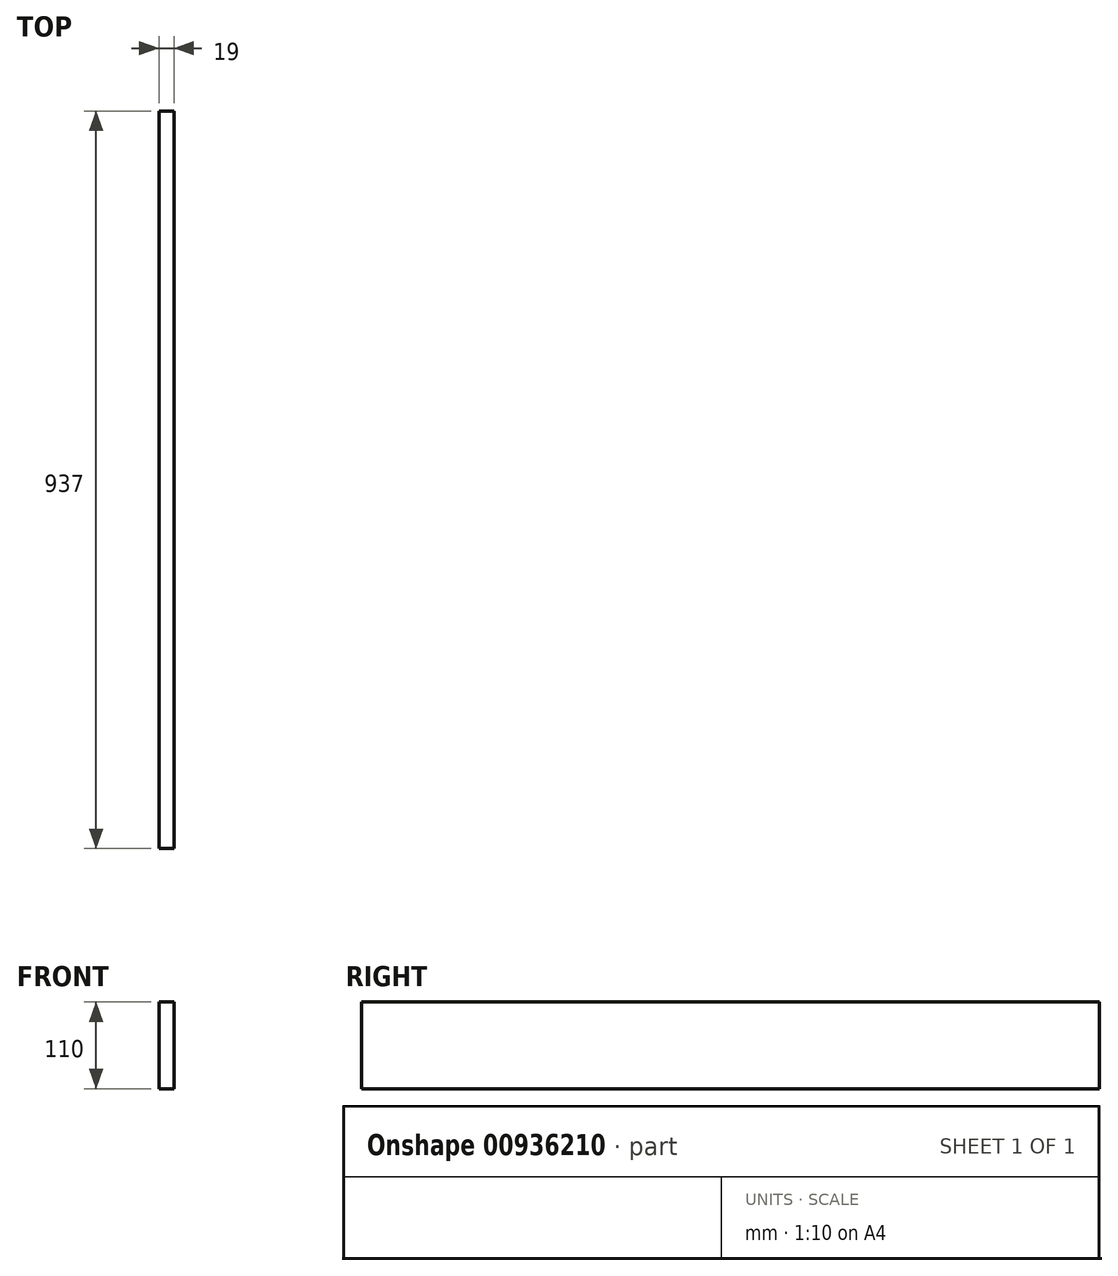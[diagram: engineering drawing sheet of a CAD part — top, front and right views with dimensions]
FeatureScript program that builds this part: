
annotation { "Feature Type Name" : "Feature", "Feature Type Description" : "" }
export const myFeature = defineFeature(function(context is Context, id is Id, definition is map)
    precondition{}
    {
        {
            var Q0;
            Q0=qCreatedBy(makeId("Front.planeOp"),FACE);
            var sketch = newSketch(context, id + "F0", { "sketchPlane" : qUnion([Q0])});
            skLineSegment(sketch, "E0.bottom", {"start": v(0, 0) * mm, "end": v(19, 0) * mm});
            skLineSegment(sketch, "E0.top", {"start": v(0, 110) * mm, "end": v(19, 110) * mm});
            skLineSegment(sketch, "E0.left", {"start": v(0, 0) * mm, "end": v(0, 110) * mm});
            skLineSegment(sketch, "E0.right", {"start": v(19, 0) * mm, "end": v(19, 110) * mm});
            skSolve(sketch);
        }
        {
            var Q0;
            Q0=qSketchRegion(id+"F0",true);
            extrude(context, id + "F1", {"entities" : qUnion([Q0]), "depth" : 937 * mm, "offsetDistance" : 25 * mm});
        }
    });
